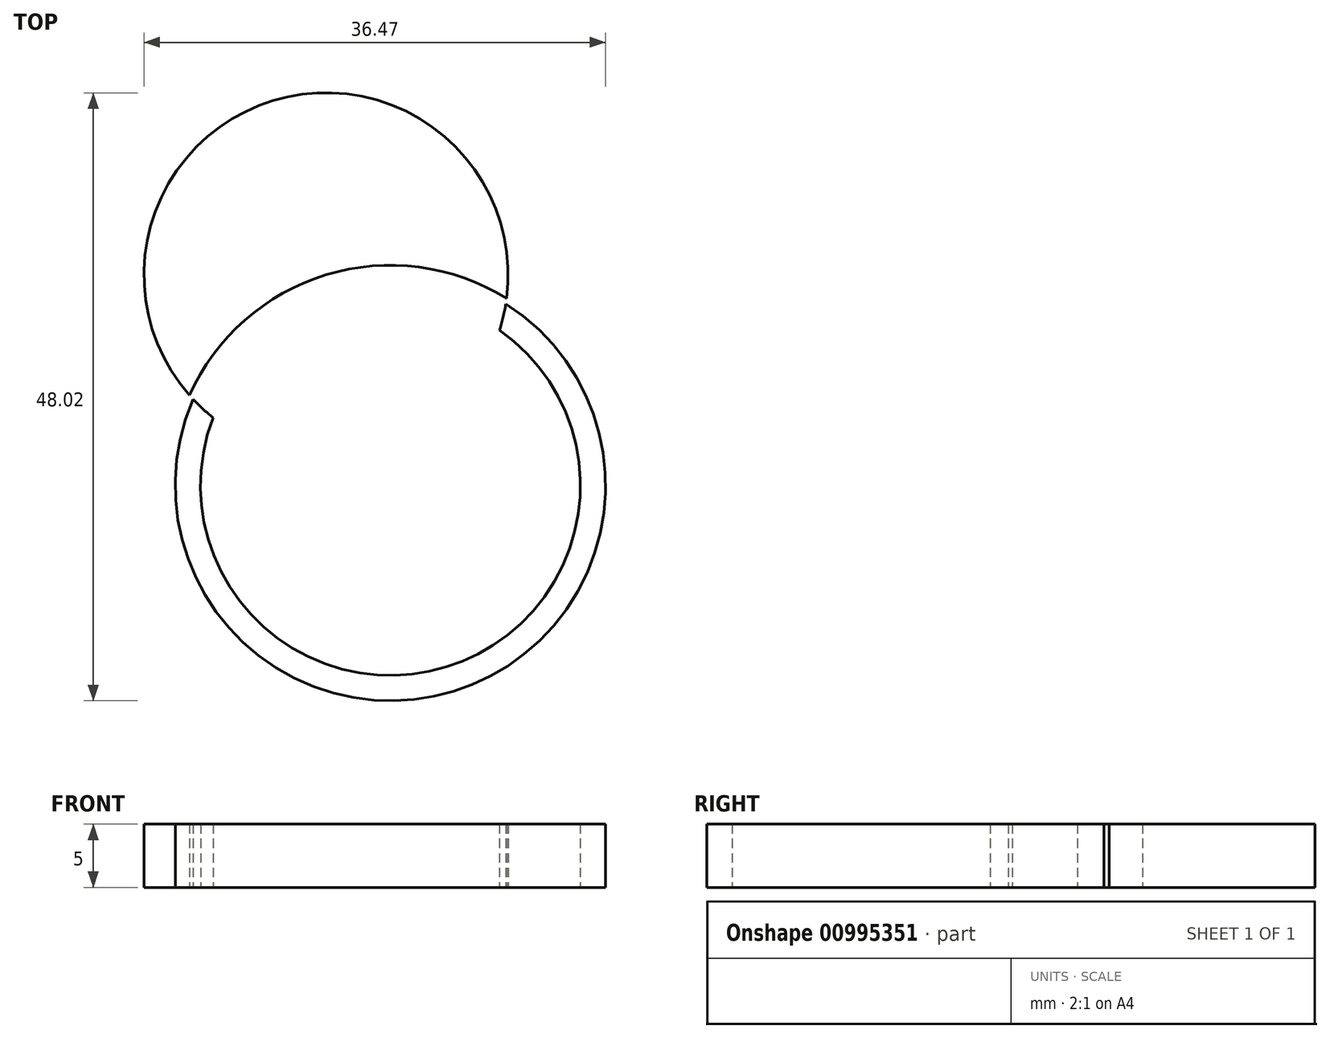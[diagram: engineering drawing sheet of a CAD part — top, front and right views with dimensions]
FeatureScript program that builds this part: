
annotation { "Feature Type Name" : "Feature", "Feature Type Description" : "" }
export const myFeature = defineFeature(function(context is Context, id is Id, definition is map)
    precondition{}
    {
        {
            var Q0;
            Q0=qCreatedBy(makeId("Top.planeOp"),FACE);
            var sketch = newSketch(context, id + "F0", { "sketchPlane" : qUnion([Q0])});
            skCircle(sketch, "E0", {"center": v(0, 0) * mm, "radius": 15 * mm});
            skCircle(sketch, "E1", {"center": v(0, 0) * mm, "radius": 17 * mm});
            skCircle(sketch, "E2", {"center": v(0, 0) * mm, "radius": 17.4 * mm});
            skCircle(sketch, "E3", {"center": v(-5.08, 16.64) * mm, "radius": 14.38 * mm});
            skSolve(sketch);
        }
        {
            var Q0;
            {var subQ0=sQuery(id+"F0.wireOp",EDGE,"E3");var subQ1=sQuery(id+"F0.wireOp",EDGE,"E2");var subQ2=makeQuery(id+"F0.imprint","INTERSECT",VERTEX,{"disambiguationData":[OD(0.0)],"derivedFrom":[subQ1,subQ0]});Q0=makeQuery(id+"F0.imprint","IMPRINT",FACE,{"disambiguationData":[TD([[makeQuery(id+"F0.imprint","IMPRINT",EDGE,{"disambiguationData":[TD([[subQ2,1.0]])],"derivedFrom":subQ1}),-1.0]])]});}
            var Q1;
            {var subQ0=sQuery(id+"F0.wireOp",EDGE,"E3");var subQ1=sQuery(id+"F0.wireOp",EDGE,"E0");var subQ2=makeQuery(id+"F0.imprint","INTERSECT",VERTEX,{"disambiguationData":[OD(0.0)],"derivedFrom":[subQ1,subQ0]});Q1=makeQuery(id+"F0.imprint","IMPRINT",FACE,{"disambiguationData":[TD([[makeQuery(id+"F0.imprint","IMPRINT",EDGE,{"disambiguationData":[TD([[subQ2,-1.0]])],"derivedFrom":subQ1}),-1.0]])]});}
            extrude(context, id + "F1", {"entities" : qUnion([Q0, Q1]), "depth" : 5 * mm, "offsetDistance" : 25 * mm});
        }
    });
